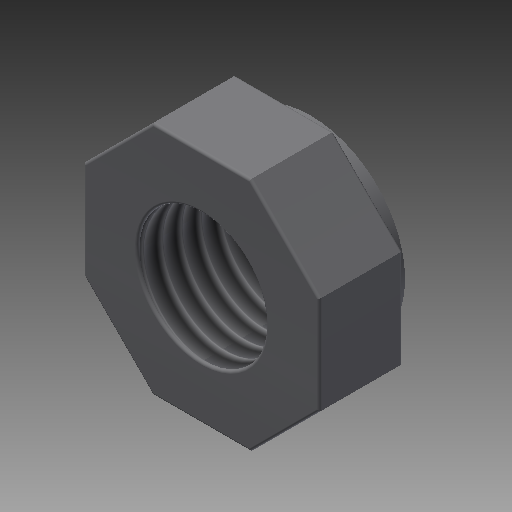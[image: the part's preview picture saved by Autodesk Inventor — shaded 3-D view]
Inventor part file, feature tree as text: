
AUTODESK INVENTOR PART (.ipt)
format: ipt  version: 2019 (Build 230136000, 136)  size: 160,256 bytes
history: native  units: mm
features: extrude x2, sketch x2, fillet x1, thread x1
ambient origin geometry x8: Origin, YZ Plane, XZ Plane, XY Plane, X Axis, Y Axis, Z Axis, Center Point
bodies: Solid1 (feature_tree)
feature tree (6):
  extrude  "Extrusion1"  Depth=10.0mm
  extrude  "Extrusion2"  Depth=10.0mm
  fillet  "Fillet1"  Radius=2.0mm
  thread  "Thread1"  [1 undecoded]
  sketch  "Sketch1"  dims[d0=18.293mm d1=10.0mm]
  sketch  "Sketch2"  dims[d2=6.48mm d3=0.0mm d4=14.65mm d5=2.0mm d6=0.0mm d7=0.2mm d8=10.0mm d9=0.0mm]
note: 1 required parameter value undecoded (feature->parameter linkage not recoverable at this tier; creation-order binding heuristic only, values carry confidence <= 0.55)
